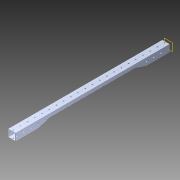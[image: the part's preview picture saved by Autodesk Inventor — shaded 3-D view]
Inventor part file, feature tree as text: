
AUTODESK INVENTOR PART (.ipt)
format: ipt  version: 2014 (Build 180170000, 170)  size: 1,335,808 bytes
history: native  units: in
note: dims shown in document units (in); Inventor stores cm internally (conversion verified against a paired STEP export)
features: extrude x3, sketch x3, pattern_circular x1, other x1, plane x1, imported_body x1, projected_geometry x1
ambient origin geometry x8: Origin, YZ Plane, XZ Plane, XY Plane, X Axis, Y Axis, Z Axis, Center Point
bodies: Body1 (feature_tree)
feature tree (11):
  pattern_circular  "CirPattern2"
  other  "217-3426-STEP1"
  plane  "Work Plane1"
  extrude  "Extrusion1"  Depth=3937.0079in TaperAngle=0.0deg
  extrude  "Extrusion2"  Depth=21.375in
  extrude  "Extrusion3"  Depth=1.0in TaperAngle=0.0deg
  imported_body  "Base1"
  sketch  "Sketch1"  dims[d0=-22.0in d1=3937.0079in d2=0.0in]
  sketch  "Sketch3"  dims[d3=21.375in d4=11.0in]
  projected_geometry  "Projected Loop1"
  sketch  "Sketch4"  dims[d5=2.0in d6=0.0in d7=1.0in d8=0.0in d9=1.5in d10=1.5in]
